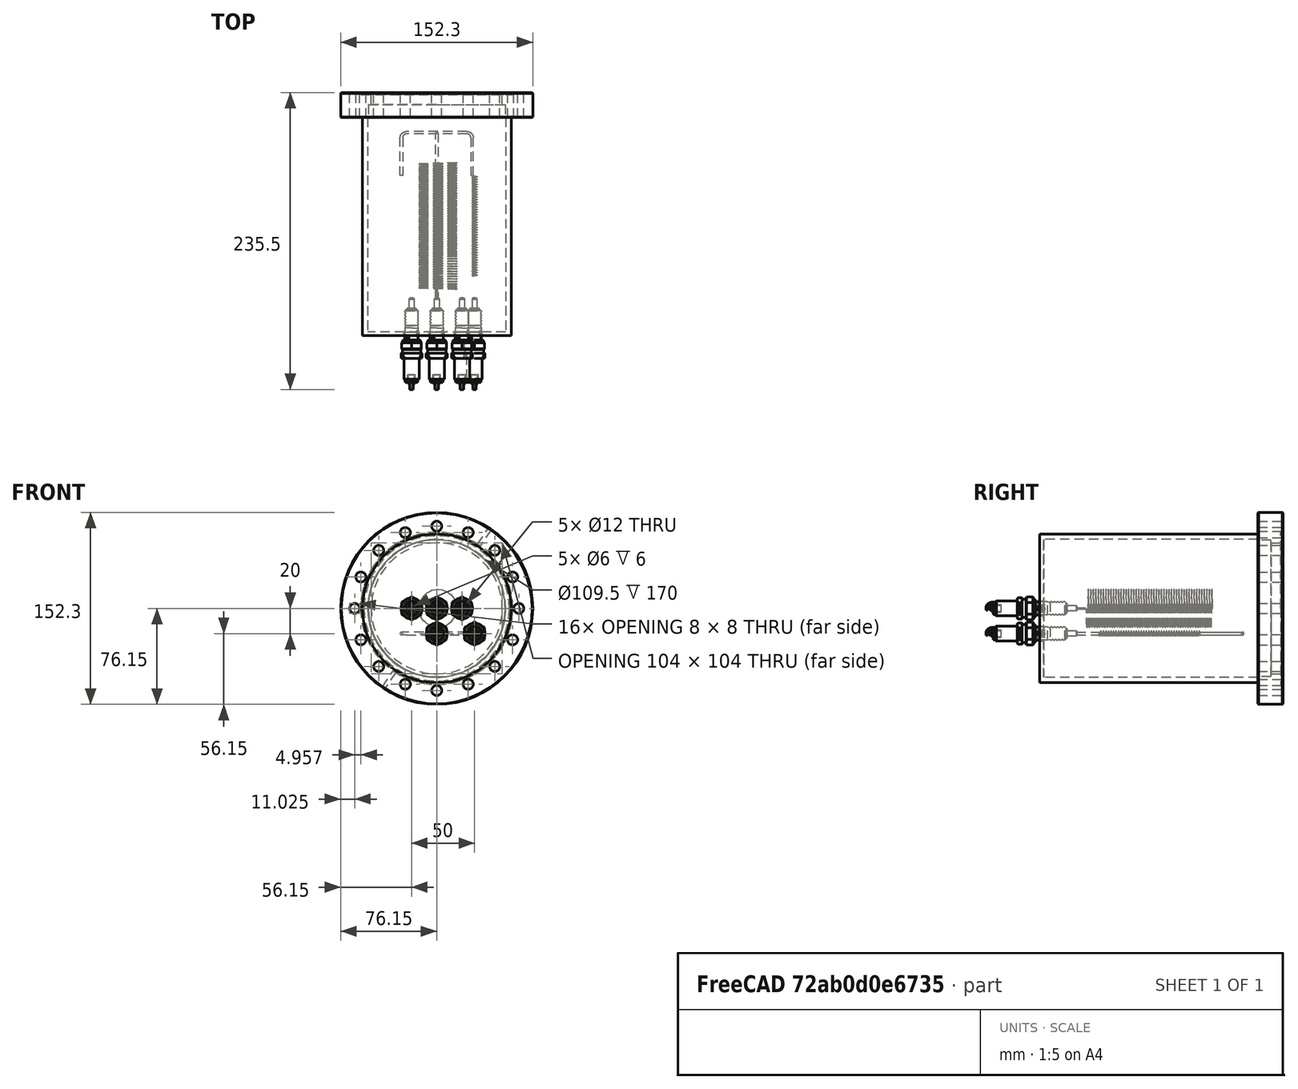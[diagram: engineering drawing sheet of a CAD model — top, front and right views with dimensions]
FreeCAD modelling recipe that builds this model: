
FCSTD DOCUMENT  (FreeCAD 1.0R39285 (Git))
Label: BA_Gauge
License: All rights reserved
LicenseURL: https://en.wikipedia.org/wiki/All_rights_reserved
objects: Part::Feature×11, Part::Cylinder×5, Part::MultiFuse×4, Part::Mirroring×3, Sketcher::SketchObject×2, PartDesign::AdditiveHelix×2, PartDesign::Body×2, Part::FeaturePython×2, Part::Torus×1, Part::Cut×1
note: 39 computed .brp shape members not serialized (recipe doc carries the construction recipe); baked Part::Feature solids carry a one-line shape summary decoded from their .brp

FEATURE [Sketcher::SketchObject] Sketch
  ArcFitTolerance = 1e-06
  AttachmentSupport = -> [XY_Plane001]
  FullyConstrained = false
  MakeInternals = false
  MapMode = 5
  sketch-geometry (1):
    g0: Circle CenterX=15.0016 CenterY=0 CenterZ=0 NormalX=0 NormalY=0 NormalZ=1 AngleXU=0 Radius=0.1
  constraints (2):
    c: Diameter(g0) = 0.2
    c: PointOnObject(g0,g-1)
FEATURE [PartDesign::AdditiveHelix] AdditiveHelix
  Angle = 0
  Axis = (0,1,0)
  Base = (0,0,0)
  Growth = 0
  HasBeenEdited = true
  Height = 100
  LeftHanded = false
  Mode = 0
  Outside = false
  Pitch = 2
  Profile = -> Sketch
  ReferenceAxis = -> Sketch [V_Axis]
  Refine = true
  Suppressed = false
  Tolerance = 0.1
  Turns = 50
FEATURE [PartDesign::Body] Body001  label="AnodeGridW"
  AllowCompound = false
  Group = -> [Sketch,AdditiveHelix]
  Origin = -> Origin001
  Placement = pos=(1,0,0) rot=(0,0,1;0rad)
  Tip = -> AdditiveHelix
FEATURE [Sketcher::SketchObject] Sketch001
  ArcFitTolerance = 1e-06
  AttachmentSupport = -> [XY_Plane]
  FullyConstrained = false
  MakeInternals = false
  MapMode = 5
  sketch-geometry (1):
    g0: Circle CenterX=1.96924 CenterY=0 CenterZ=0 NormalX=0 NormalY=0 NormalZ=1 AngleXU=0 Radius=0.1
  constraints (2):
    c: Diameter(g0) = 0.2
    c: PointOnObject(g0,g-1)
FEATURE [PartDesign::AdditiveHelix] AdditiveHelix001
  Angle = 0
  Axis = (0,1,0)
  Base = (0,0,0)
  Growth = 0
  HasBeenEdited = true
  Height = 80
  LeftHanded = false
  Mode = 0
  Outside = false
  Pitch = 2
  Profile = -> Sketch001
  ReferenceAxis = -> Sketch001 [V_Axis]
  Refine = true
  Suppressed = false
  Tolerance = 0.1
  Turns = 40
FEATURE [PartDesign::Body] Body  label="Fil1"
  AllowCompound = false
  Group = -> [Sketch001,AdditiveHelix001]
  Origin = -> Origin
  Placement = pos=(-30,10,-20) rot=(0,0,1;0rad)
  Tip = -> AdditiveHelix001
FEATURE [Part::Cylinder] Cylinder  label="CollectorW"
  Angle = 360
  AttacherType = Attacher::AttachEngine3D
  FirstAngle = 0
  Height = 88
  Placement = pos=(0,80,0) rot=(1,0,0;1.5708rad)
  Radius = 0.5
  SecondAngle = 0
FEATURE [Part::Mirroring] Part__Mirroring  label="CathodeFilamentW"
  Base = (0,0,0)
  Normal = (1,0,0)
  Source = -> Body
FEATURE [Part::Cylinder] Cylinder002  label="Collector002"
  Angle = 360
  AttacherType = Attacher::AttachEngine3D
  FirstAngle = 0
  Height = 30
  Placement = pos=(-28,120,0) rot=(1,0,0;1.5708rad)
  Radius = 1
  SecondAngle = 0
FEATURE [Part::Mirroring] Part__Mirroring002  label="TopSupportSS"
  Base = (0,0,0)
  Normal = (1,0,0)
  Source = -> Cylinder002
FEATURE [Part::Cylinder] Cylinder004  label="Cylinder"
  Angle = 360
  AttacherType = Attacher::AttachEngine3D
  FirstAngle = 0
  Height = 48
  Placement = pos=(-24,124,0) rot=(0,1,0;1.5708rad)
  Radius = 1
  SecondAngle = 0
FEATURE [Part::Feature] Part__Feature009  label="CollectorSparkPlug"
  Placement = pos=(0,-55,0) rot=(0,0,1;4.71239rad)
  shape: bbox 163.5 x 72.51 x 18.14 mm, 412 faces (baked)
FEATURE [Part::Torus] Torus
  Angle1 = -180
  Angle2 = 180
  Angle3 = 90
  AttacherType = Attacher::AttachEngine3D
  Placement = pos=(24,120,0) rot=(0,0,1;0rad)
  Radius1 = 4
  Radius2 = 1
FEATURE [Part::Mirroring] Part__Mirroring003  label="Torus (Mirror #3)"
  Base = (0,0,0)
  Normal = (1,0,0)
  Source = -> Torus
FEATURE [Part::MultiFuse] Fusion  label="CathodeTopSS"
  Placement = pos=(0,0,-20) rot=(0,0,1;0rad)
  Shapes = -> [Part__Mirroring003,Torus,Cylinder002,Part__Mirroring002,Cylinder004]
FEATURE [Part::Cylinder] Cylinder005
  Angle = 360
  AttacherType = Attacher::AttachEngine3D
  FirstAngle = 0
  Height = 132
  Placement = pos=(0,124,-20) rot=(1,0,0;1.5708rad)
  Radius = 1
  SecondAngle = 0
FEATURE [Part::Feature] Part__Feature010  label="AnodeSparkPlug"
  Placement = pos=(30,-55,-20) rot=(0,0,1;4.71239rad)
  shape: bbox 163.5 x 72.51 x 18.14 mm, 412 faces (baked)
FEATURE [Part::Feature] Part__Feature011  label="CathodeSparkPlug"
  Placement = pos=(20,-55,0) rot=(0,0,1;4.71239rad)
  shape: bbox 163.5 x 72.51 x 18.14 mm, 412 faces (baked)
FEATURE [Part::Feature] Part__Feature012  label="AnodeSparkPlug001"
  Placement = pos=(0,-55,-20) rot=(0,0,1;4.71239rad)
  shape: bbox 163.5 x 72.51 x 18.14 mm, 412 faces (baked)
FEATURE [Part::Feature] Part__Feature013  label="CathodeSparkPlug001"
  Placement = pos=(-20,-55,0) rot=(0,0,1;4.71239rad)
  shape: bbox 163.5 x 72.51 x 18.14 mm, 412 faces (baked)
FEATURE [Part::Cylinder] Cylinder006
  Angle = 360
  AttacherType = Attacher::AttachEngine3D
  FirstAngle = 0
  Height = 3
  Placement = pos=(0,-34,0) rot=(1,0,0;1.5708rad)
  Radius = 59
  SecondAngle = 0
FEATURE [Part::FeaturePython] Tube  # WARN: FeaturePython — macro-defined, semantics opaque (R4)
  AttacherType = Attacher::AttachEngine3D
  Height = 170
  InnerRadius = 54.75
  OuterRadius = 59
  Placement = pos=(0,136,0) rot=(1,0,0;1.5708rad)
FEATURE [Part::Feature] Part__Feature014  label="CollectorSparkPlug001"
  Placement = pos=(0,-55,0) rot=(0,0,1;4.71239rad)
  shape: bbox 163.5 x 72.51 x 18.14 mm, 412 faces (baked)
FEATURE [Part::Feature] Part__Feature015  label="AnodeSparkPlug002"
  Placement = pos=(30,-55,-20) rot=(0,0,1;4.71239rad)
  shape: bbox 163.5 x 72.51 x 18.14 mm, 412 faces (baked)
FEATURE [Part::Feature] Part__Feature016  label="CathodeSparkPlug002"
  Placement = pos=(20,-55,0) rot=(0,0,1;4.71239rad)
  shape: bbox 163.5 x 72.51 x 18.14 mm, 412 faces (baked)
FEATURE [Part::Feature] Part__Feature017  label="AnodeSparkPlug003"
  Placement = pos=(0,-55,-20) rot=(0,0,1;4.71239rad)
  shape: bbox 163.5 x 72.51 x 18.14 mm, 412 faces (baked)
FEATURE [Part::Feature] Part__Feature018  label="CathodeSparkPlug003"
  Placement = pos=(-20,-55,0) rot=(0,0,1;4.71239rad)
  shape: bbox 163.5 x 72.51 x 18.14 mm, 412 faces (baked)
FEATURE [Part::MultiFuse] Fusion001
  Placement = pos=(0,28,0) rot=(0,0,1;0rad)
  Shapes = -> [Part__Feature018,Part__Feature014,Part__Feature015,Part__Feature016,Part__Feature017]
FEATURE [Part::Cut] Cut
  Base = -> Cylinder006
  Tool = -> Fusion001
FEATURE [Part::Feature] Part__Feature  label="190094"
  shape: bbox 152.3 x 19.8 x 152.3 mm, 298 faces (baked)
FEATURE [Part::FeaturePython] Tube001  # WARN: FeaturePython — macro-defined, semantics opaque (R4)
  AttacherType = Attacher::AttachEngine3D
  Height = 18
  InnerRadius = 74
  OuterRadius = 76.15
  Placement = pos=(0,19,0) rot=(1,0,0;1.5708rad)
FEATURE [Part::MultiFuse] Fusion002
  Placement = pos=(0,136,0) rot=(0,0,1;0rad)
  Shapes = -> [Part__Feature,Tube001]
FEATURE [Part::MultiFuse] Fusion003  label="DN100CF_Flange"
  Shapes = -> [Fusion002,Cut,Tube]
